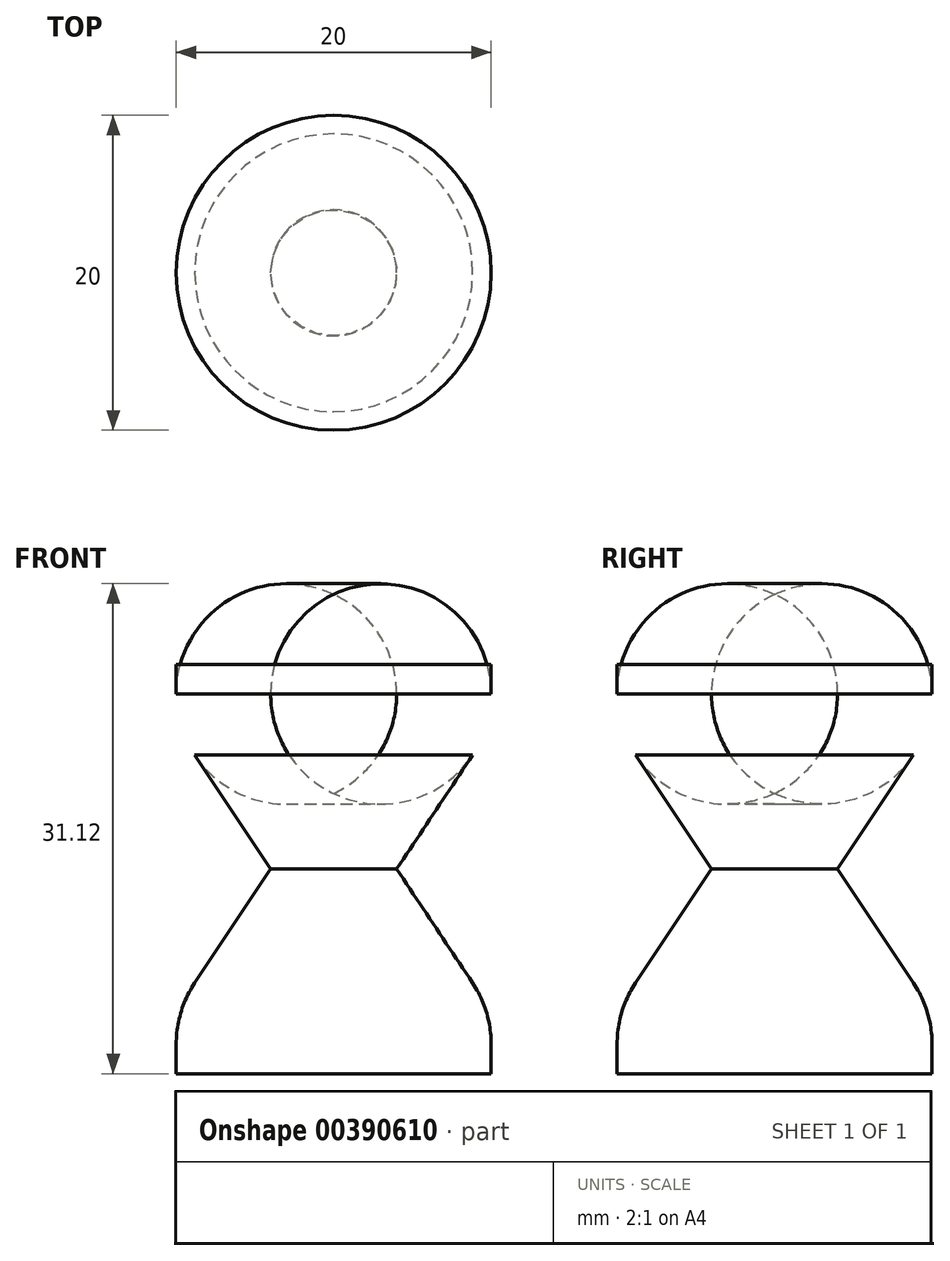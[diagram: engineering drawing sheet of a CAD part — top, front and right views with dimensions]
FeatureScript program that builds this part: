
annotation { "Feature Type Name" : "Feature", "Feature Type Description" : "" }
export const myFeature = defineFeature(function(context is Context, id is Id, definition is map)
    precondition{}
    {
        {
            var Q0;
            Q0=qCreatedBy(makeId("Top.planeOp"),FACE);
            cPlane(context, id + "F0", {"entities" : qUnion([Q0]), "cplaneType" : CPlaneType.OFFSET, "offset" : 9 * mm, "width" : 150 * mm, "height" : 150 * mm});
        }
        {
            var Q0;
            Q0=qCreatedBy(id+"F0.planeOp",FACE);
            var sketch = newSketch(context, id + "F1", { "sketchPlane" : qUnion([Q0])});
            skCircle(sketch, "E0", {"center": v(0, 0) * mm, "radius": 10 * mm});
            skSolve(sketch);
        }
        {
            var Q0;
            Q0=qCreatedBy(makeId("Top.planeOp"),FACE);
            var sketch = newSketch(context, id + "F2", { "sketchPlane" : qUnion([Q0])});
            skCircle(sketch, "E1", {"center": v(0, 0) * mm, "radius": 4 * mm});
            skSolve(sketch);
        }
        {
            var Q0;
            Q0=makeQuery(id+"F1.imprint","IMPRINT",FACE,{"disambiguationData":[TD([[makeQuery(id+"F1.imprint","IMPRINT",EDGE,{"derivedFrom":sQuery(id+"F1.wireOp",EDGE,"E0")}),1.0]])]});
            var Q1;
            Q1=makeQuery(id+"F2.imprint","IMPRINT",FACE,{"disambiguationData":[TD([[makeQuery(id+"F2.imprint","IMPRINT",EDGE,{"derivedFrom":sQuery(id+"F2.wireOp",EDGE,"E1")}),1.0]])]});
            loft(context, id + "F3", {"sheetProfilesArray" : [{ "sheetProfileEntities" : qUnion([Q0]) }, { "sheetProfileEntities" : qUnion([Q1]) }]});
        }
        {
            var Q0;
            Q0=makeQuery(id+"F3.opLoft","SWEPT_BODY",BODY,{"disambiguationData":[OSD([makeQuery(id+"F1.imprint","IMPRINT",FACE,{"disambiguationData":[TD([[makeQuery(id+"F1.imprint","IMPRINT",EDGE,{"derivedFrom":sQuery(id+"F1.wireOp",EDGE,"E0")}),1.0]])]}),makeQuery(id+"F2.imprint","IMPRINT",FACE,{"disambiguationData":[TD([[makeQuery(id+"F2.imprint","IMPRINT",EDGE,{"derivedFrom":sQuery(id+"F2.wireOp",EDGE,"E1")}),1.0]])]})])]});
            var Q1;
            Q1=qCreatedBy(makeId("Top.planeOp"),FACE);
            mirror(context, id + "F4", {"operationType" : NewBodyOperationType.ADD, "entities" : qUnion([Q0]), "mirrorPlane" : qUnion([Q1])});
        }
        {
            var Q0;
            Q0=makeQuery(id+"F4.opPattern","COPY",FACE,{"derivedFrom":makeQuery(id+"F3.opLoft","CAP_FACE",FACE,{"disambiguationData":[OSD([makeQuery(id+"F1.imprint","IMPRINT",FACE,{"disambiguationData":[TD([[makeQuery(id+"F1.imprint","IMPRINT",EDGE,{"derivedFrom":sQuery(id+"F1.wireOp",EDGE,"E0")}),1.0]])]})])],"isStart":true}),"instanceName":"1"});
            extrude(context, id + "F5", {"entities" : qUnion([Q0]), "operationType" : NewBodyOperationType.ADD, "depth" : 4 * mm, "offsetDistance" : 25 * mm});
        }
        {
            var Q0;
            Q0=makeQuery(id+"F3.opLoft","CAP_FACE",FACE,{"disambiguationData":[OSD([makeQuery(id+"F1.imprint","IMPRINT",FACE,{"disambiguationData":[TD([[makeQuery(id+"F1.imprint","IMPRINT",EDGE,{"derivedFrom":sQuery(id+"F1.wireOp",EDGE,"E0")}),1.0]])]})])],"isStart":true});
            extrude(context, id + "F6", {"entities" : qUnion([Q0]), "operationType" : NewBodyOperationType.ADD, "depth" : 4 * mm, "offsetDistance" : 25 * mm});
        }
        {
            var Q0;
            {var subQ0=makeQuery(id+"F3.opLoft","MID_CAP_EDGE",EDGE,{"disambiguationData":[OSD([sQuery(id+"F2.wireOp",EDGE,"E1")])],"capPos":1.0});Q0=makeQuery(id+"F4.boolean.opBoolean","MERGE",EDGE,{"derivedFrom":[subQ0,makeQuery(id+"F4.opPattern","COPY",EDGE,{"derivedFrom":subQ0,"instanceName":"1"})]});}
            var Q1;
            {var subQ0=sQuery(id+"F1.wireOp",EDGE,"E0");Q1=makeQuery(id+"F5.boolean.opBoolean","MERGE",EDGE,{"derivedFrom":[makeQuery(id+"F4.opPattern","COPY",EDGE,{"derivedFrom":makeQuery(id+"F3.opLoft","MID_CAP_EDGE",EDGE,{"disambiguationData":[OSD([subQ0])],"capPos":0.0}),"instanceName":"1"}),makeQuery(id+"F5.opExtrude","CAP_EDGE",EDGE,{"disambiguationData":[OSD([subQ0])],"isStart":true})]});}
            var Q2;
            {var subQ0=sQuery(id+"F1.wireOp",EDGE,"E0");Q2=makeQuery(id+"F6.boolean.opBoolean","MERGE",EDGE,{"derivedFrom":[makeQuery(id+"F3.opLoft","MID_CAP_EDGE",EDGE,{"disambiguationData":[OSD([subQ0])],"capPos":0.0}),makeQuery(id+"F6.opExtrude","CAP_EDGE",EDGE,{"disambiguationData":[OSD([subQ0])],"isStart":true})]});}
            fillet(context, id + "F7", {"entities" : qUnion([Q0, Q1, Q2]), "tangentPropagation" : true, "radius" : 7 * mm, "defaultsChanged" : false, "vertexSettings" : [], "allowEdgeOverflow" : false});
        }
    });
